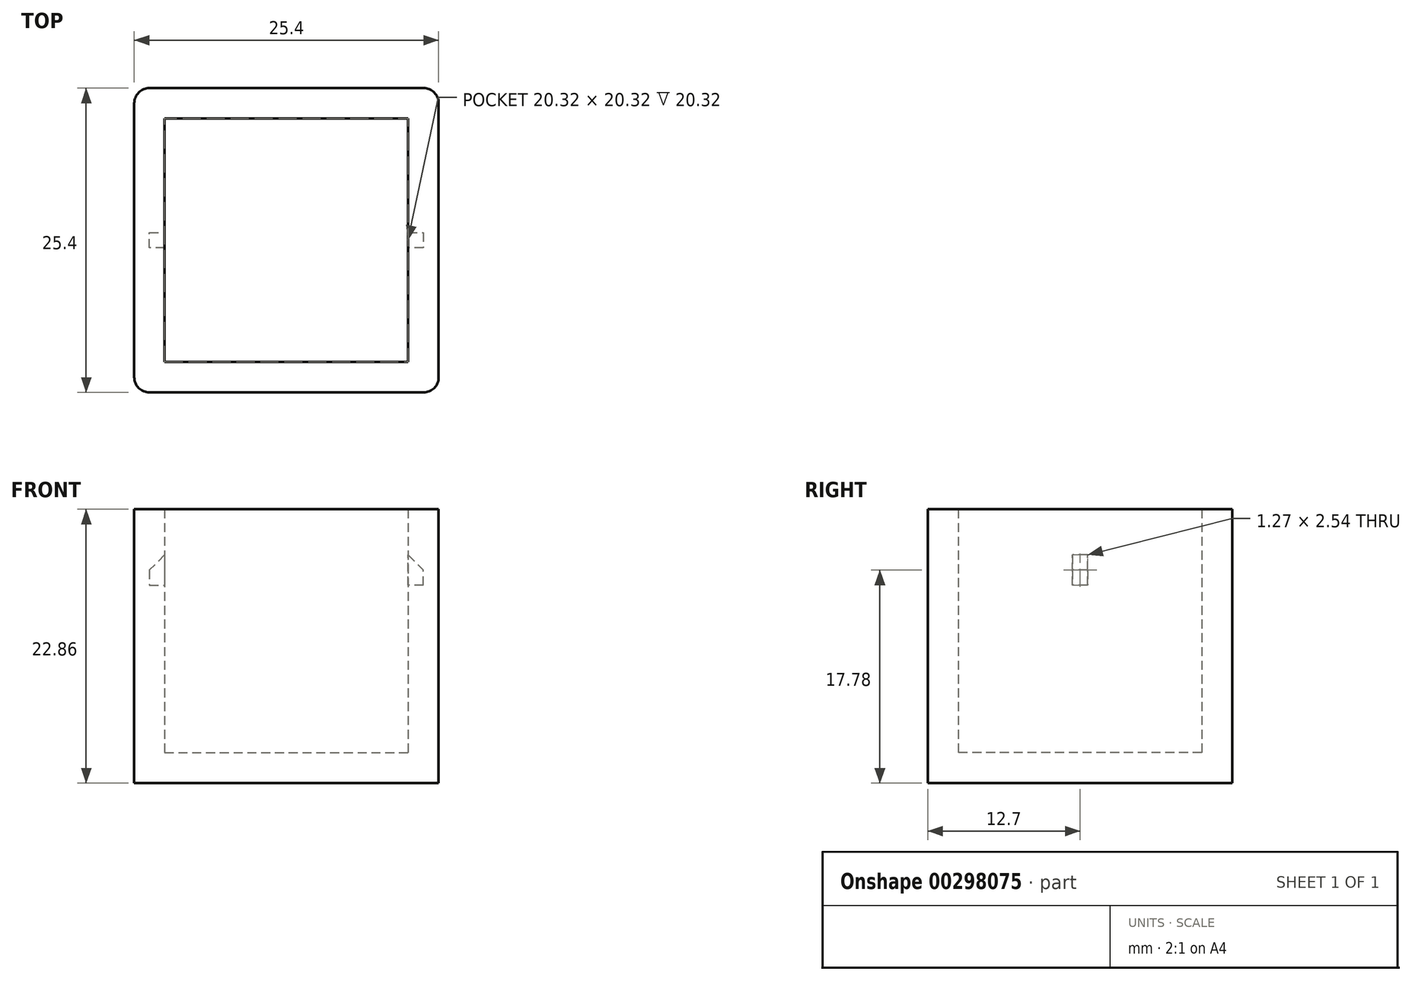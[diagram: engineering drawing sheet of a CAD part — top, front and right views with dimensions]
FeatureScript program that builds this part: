
annotation { "Feature Type Name" : "Feature", "Feature Type Description" : "" }
export const myFeature = defineFeature(function(context is Context, id is Id, definition is map)
    precondition{}
    {
        {
            var Q0;
            Q0=qCreatedBy(makeId("Top.planeOp"),FACE);
            var sketch = newSketch(context, id + "F0", { "sketchPlane" : qUnion([Q0])});
            skLineSegment(sketch, "E0.bottom", {"start": v(-10.16, 10.16) * mm, "end": v(10.16, 10.16) * mm});
            skLineSegment(sketch, "E0.top", {"start": v(-10.16, -10.16) * mm, "end": v(10.16, -10.16) * mm});
            skLineSegment(sketch, "E0.left", {"start": v(-10.16, 10.16) * mm, "end": v(-10.16, -10.16) * mm});
            skLineSegment(sketch, "E0.right", {"start": v(10.16, 10.16) * mm, "end": v(10.16, -10.16) * mm});
            skPoint(sketch, "E0.middle", {"position": v(0, 0) * mm});
            skLineSegment(sketch, "E1.bottom", {"start": v(-12.7, 12.7) * mm, "end": v(12.7, 12.7) * mm});
            skLineSegment(sketch, "E1.top", {"start": v(-12.7, -12.7) * mm, "end": v(12.7, -12.7) * mm});
            skLineSegment(sketch, "E1.left", {"start": v(-12.7, 12.7) * mm, "end": v(-12.7, -12.7) * mm});
            skLineSegment(sketch, "E1.right", {"start": v(12.7, 12.7) * mm, "end": v(12.7, -12.7) * mm});
            skSolve(sketch);
        }
        {
            var Q0;
            Q0=makeQuery(id+"F0.imprint","IMPRINT",FACE,{"disambiguationData":[TD([[makeQuery(id+"F0.imprint","IMPRINT",EDGE,{"derivedFrom":sQuery(id+"F0.wireOp",EDGE,"E0.bottom")}),-1.0]])]});
            extrude(context, id + "F1", {"entities" : qUnion([Q0]), "depth" : 2.54 * mm});
        }
        {
            var Q0;
            Q0 = qSketchRegion(id + "F0", true);
            extrude(context, id + "F2", {"entities" : qUnion([Q0]), "operationType" : NewBodyOperationType.ADD, "depth" : 22.86 * mm});
        }
        {
            var Q0;
            Q0=makeQuery(id+"F2.opExtrude","SWEPT_FACE",FACE,{"disambiguationData":[OSD([sQuery(id+"F0.wireOp",EDGE,"E0.left")])]});
            var sketch = newSketch(context, id + "F3", { "sketchPlane" : qUnion([Q0])});
            skLineSegment(sketch, "E2.bottom", {"start": v(-0.64, 19.05) * mm, "end": v(0.63, 19.05) * mm});
            skLineSegment(sketch, "E2.top", {"start": v(-0.64, 16.51) * mm, "end": v(0.63, 16.51) * mm});
            skLineSegment(sketch, "E2.left", {"start": v(-0.64, 19.05) * mm, "end": v(-0.64, 16.51) * mm});
            skLineSegment(sketch, "E2.right", {"start": v(0.63, 19.05) * mm, "end": v(0.63, 16.51) * mm});
            skPoint(sketch, "E2.middle", {"position": v(0, 17.78) * mm});
            skLineSegment(sketch, "E3.bottom", {"start": v(-0.32, 17.14) * mm, "end": v(0.32, 17.14) * mm});
            skLineSegment(sketch, "E3.top", {"start": v(-0.32, 18.41) * mm, "end": v(0.32, 18.41) * mm});
            skLineSegment(sketch, "E3.left", {"start": v(-0.32, 17.14) * mm, "end": v(-0.32, 18.41) * mm});
            skLineSegment(sketch, "E3.right", {"start": v(0.32, 17.14) * mm, "end": v(0.32, 18.41) * mm});
            skSolve(sketch);
        }
        {
            var Q0;
            Q0=makeQuery(id+"F3.imprint","IMPRINT",FACE,{"disambiguationData":[TD([[makeQuery(id+"F3.imprint","IMPRINT",EDGE,{"derivedFrom":sQuery(id+"F3.wireOp",EDGE,"E2.bottom")}),-1.0]])]});
            var Q1;
            Q1=makeQuery(id+"F3.imprint","IMPRINT",FACE,{"disambiguationData":[TD([[makeQuery(id+"F3.imprint","IMPRINT",EDGE,{"derivedFrom":sQuery(id+"F3.wireOp",EDGE,"E3.bottom")}),1.0]])]});
            extrude(context, id + "F4", {"entities" : qUnion([Q0, Q1]), "operationType" : NewBodyOperationType.REMOVE, "oppositeDirection" : true, "depth" : 1.27 * mm});
        }
        {
            var Q0;
            Q0=makeQuery(id+"F4.boolean.opBoolean","COPY",EDGE,{"derivedFrom":makeQuery(id+"F4.opExtrude","CAP_EDGE",EDGE,{"disambiguationData":[OSD([sQuery(id+"F3.wireOp",EDGE,"E2.bottom")])],"isStart":false})});
            chamfer(context, id + "F5", {"entities" : qUnion([Q0]), "width" : 1.27 * mm, "tangentPropagation" : true});
        }
        {
            var Q0;
            Q0=makeQuery(id+"F2.opExtrude","SWEPT_FACE",FACE,{"disambiguationData":[OSD([sQuery(id+"F0.wireOp",EDGE,"E0.right")])]});
            var sketch = newSketch(context, id + "F6", { "sketchPlane" : qUnion([Q0])});
            skLineSegment(sketch, "E4.bottom", {"start": v(-0.63, 16.51) * mm, "end": v(0.64, 16.51) * mm});
            skLineSegment(sketch, "E4.top", {"start": v(-0.63, 19.05) * mm, "end": v(0.64, 19.05) * mm});
            skLineSegment(sketch, "E4.left", {"start": v(-0.63, 16.51) * mm, "end": v(-0.63, 19.05) * mm});
            skLineSegment(sketch, "E4.right", {"start": v(0.64, 16.51) * mm, "end": v(0.64, 19.05) * mm});
            skPoint(sketch, "E4.middle", {"position": v(0, 17.78) * mm});
            skSolve(sketch);
        }
        {
            var Q0;
            Q0 = qSketchRegion(id + "F6", true);
            extrude(context, id + "F7", {"entities" : qUnion([Q0]), "operationType" : NewBodyOperationType.REMOVE, "oppositeDirection" : true, "depth" : 1.27 * mm});
        }
        {
            var Q0;
            Q0=makeQuery(id+"F7.boolean.opBoolean","COPY",EDGE,{"derivedFrom":makeQuery(id+"F7.opExtrude","CAP_EDGE",EDGE,{"disambiguationData":[OSD([sQuery(id+"F6.wireOp",EDGE,"E4.top")])],"isStart":false})});
            chamfer(context, id + "F8", {"entities" : qUnion([Q0]), "width" : 1.27 * mm, "tangentPropagation" : true});
        }
        {
            var Q0;
            Q0=makeQuery(id+"F2.opExtrude","SWEPT_EDGE",EDGE,{"disambiguationData":[OSD([sQuery(id+"F0.wireOp",EDGE,"E1.top"),sQuery(id+"F0.wireOp",EDGE,"E1.left")])]});
            var Q1;
            Q1=makeQuery(id+"F2.opExtrude","SWEPT_EDGE",EDGE,{"disambiguationData":[OSD([sQuery(id+"F0.wireOp",EDGE,"E1.top"),sQuery(id+"F0.wireOp",EDGE,"E1.right")])]});
            var Q2;
            Q2=makeQuery(id+"F2.opExtrude","SWEPT_EDGE",EDGE,{"disambiguationData":[OSD([sQuery(id+"F0.wireOp",EDGE,"E1.bottom"),sQuery(id+"F0.wireOp",EDGE,"E1.right")])]});
            var Q3;
            Q3=makeQuery(id+"F2.opExtrude","SWEPT_EDGE",EDGE,{"disambiguationData":[OSD([sQuery(id+"F0.wireOp",EDGE,"E1.bottom"),sQuery(id+"F0.wireOp",EDGE,"E1.left")])]});
            fillet(context, id + "F9", {"entities" : qUnion([Q0, Q1, Q2, Q3]), "radius" : 1.27 * mm, "tangentPropagation" : true, "allowEdgeOverflow" : false});
        }
    });
